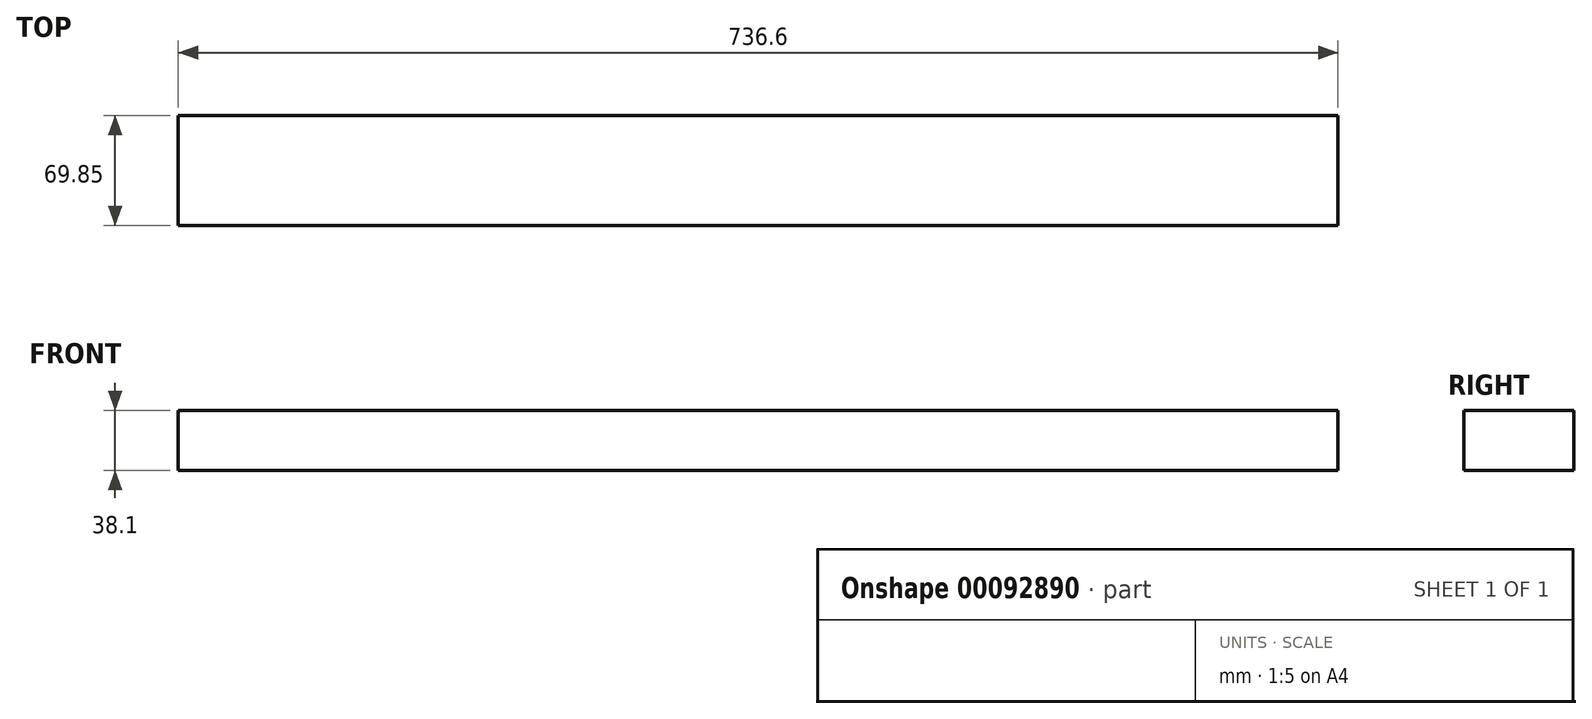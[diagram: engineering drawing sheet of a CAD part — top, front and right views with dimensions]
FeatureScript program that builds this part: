
annotation { "Feature Type Name" : "Feature", "Feature Type Description" : "" }
export const myFeature = defineFeature(function(context is Context, id is Id, definition is map)
    precondition{}
    {
        {
            var Q0;
            Q0=qCreatedBy(makeId("Front.planeOp"),FACE);
            var sketch = newSketch(context, id + "F0", { "sketchPlane" : qUnion([Q0])});
            skLineSegment(sketch, "E0.bottom", {"start": v(-766.06, -2.83) * mm, "end": v(-29.46, -2.83) * mm});
            skLineSegment(sketch, "E0.top", {"start": v(-766.06, -40.93) * mm, "end": v(-29.46, -40.93) * mm});
            skLineSegment(sketch, "E0.left", {"start": v(-766.06, -2.83) * mm, "end": v(-766.06, -40.93) * mm});
            skLineSegment(sketch, "E0.right", {"start": v(-29.46, -2.83) * mm, "end": v(-29.46, -40.93) * mm});
            skSolve(sketch);
        }
        {
            var Q0;
            Q0=makeQuery(id+"F0.imprint","IMPRINT",FACE,{"disambiguationData":[TD([[makeQuery(id+"F0.imprint","IMPRINT",EDGE,{"derivedFrom":sQuery(id+"F0.wireOp",EDGE,"E0.bottom")}),-1.0]])]});
            extrude(context, id + "F1", {"entities" : qUnion([Q0]), "depth" : 69.85 * mm});
        }
    });
